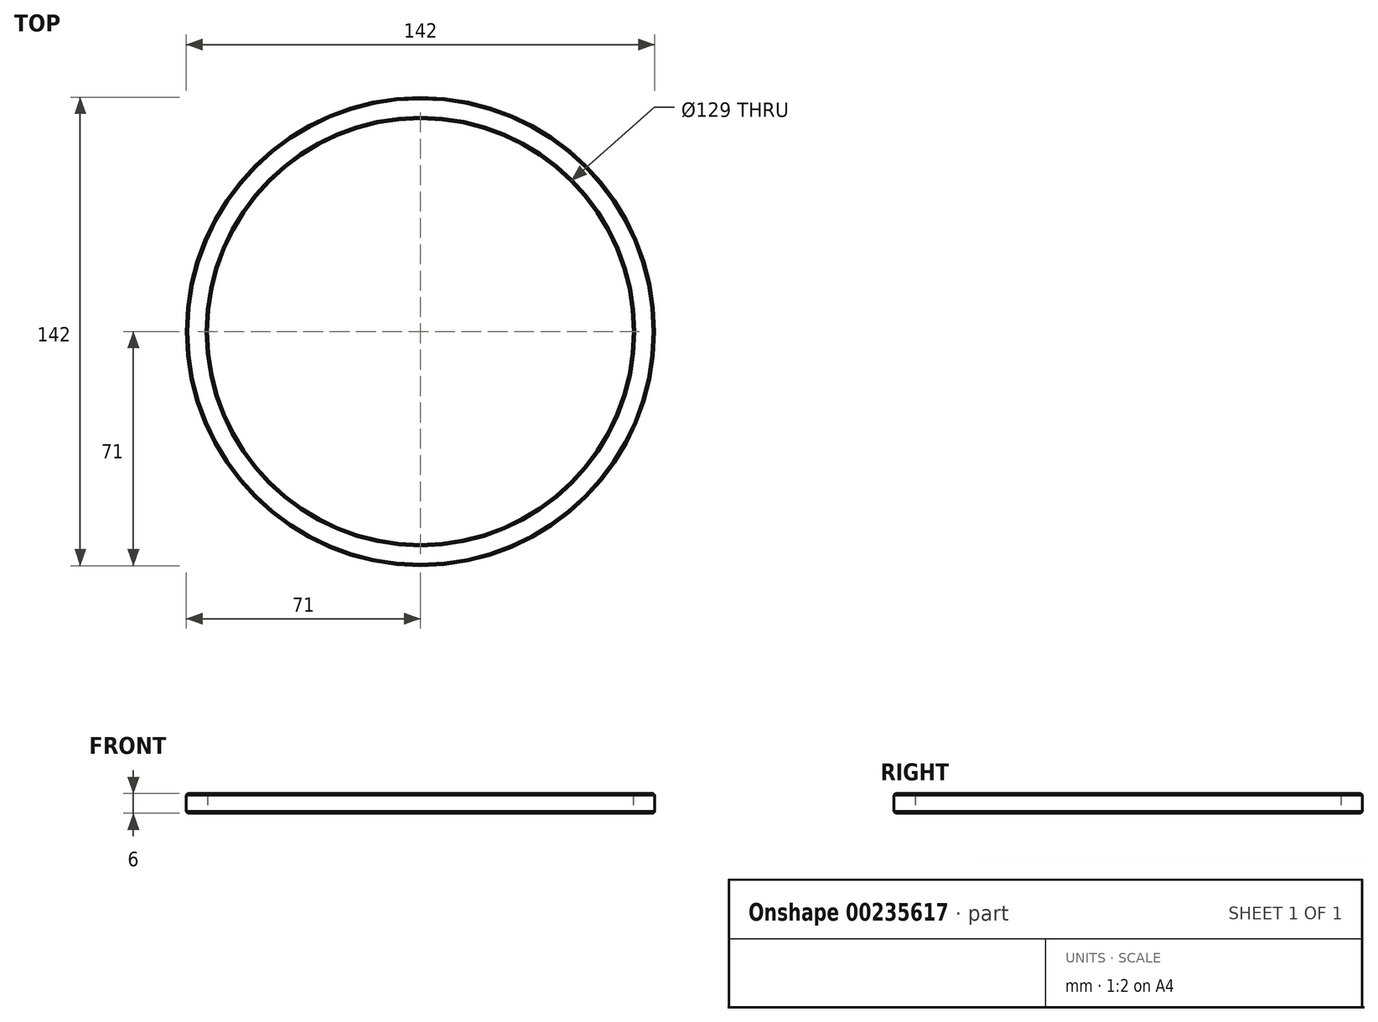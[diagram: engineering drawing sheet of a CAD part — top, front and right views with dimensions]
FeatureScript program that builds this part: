
annotation { "Feature Type Name" : "Feature", "Feature Type Description" : "" }
export const myFeature = defineFeature(function(context is Context, id is Id, definition is map)
    precondition{}
    {
        {
            var Q0;
            Q0=qCreatedBy(makeId("Top.planeOp"),FACE);
            var sketch = newSketch(context, id + "F0", { "sketchPlane" : qUnion([Q0])});
            skCircle(sketch, "E0", {"center": v(0, 0) * mm, "radius": 71 * mm});
            skCircle(sketch, "E1", {"center": v(0, 0) * mm, "radius": 64.5 * mm});
            skSolve(sketch);
        }
        {
            var Q0;
            Q0=makeQuery(id+"F0.imprint","IMPRINT",FACE,{"disambiguationData":[TD([[makeQuery(id+"F0.imprint","IMPRINT",EDGE,{"derivedFrom":sQuery(id+"F0.wireOp",EDGE,"E0")}),1.0]])]});
            extrude(context, id + "F1", {"entities" : qUnion([Q0]), "depth" : 6 * mm});
        }
        {
            var Q0;
            Q0=makeQuery(id+"F1.opExtrude","CAP_EDGE",EDGE,{"disambiguationData":[OSD([sQuery(id+"F0.wireOp",EDGE,"E0")])],"isStart":true});
            var Q1;
            Q1=makeQuery(id+"F1.opExtrude","CAP_EDGE",EDGE,{"disambiguationData":[OSD([sQuery(id+"F0.wireOp",EDGE,"E1")])],"isStart":true});
            var Q2;
            Q2=makeQuery(id+"F1.opExtrude","CAP_EDGE",EDGE,{"disambiguationData":[OSD([sQuery(id+"F0.wireOp",EDGE,"E0")])],"isStart":false});
            var Q3;
            Q3=makeQuery(id+"F1.opExtrude","CAP_EDGE",EDGE,{"disambiguationData":[OSD([sQuery(id+"F0.wireOp",EDGE,"E1")])],"isStart":false});
            chamfer(context, id + "F2", {"entities" : qUnion([Q0, Q1, Q2, Q3]), "width" : 0.5 * mm, "tangentPropagation" : true});
        }
    });
